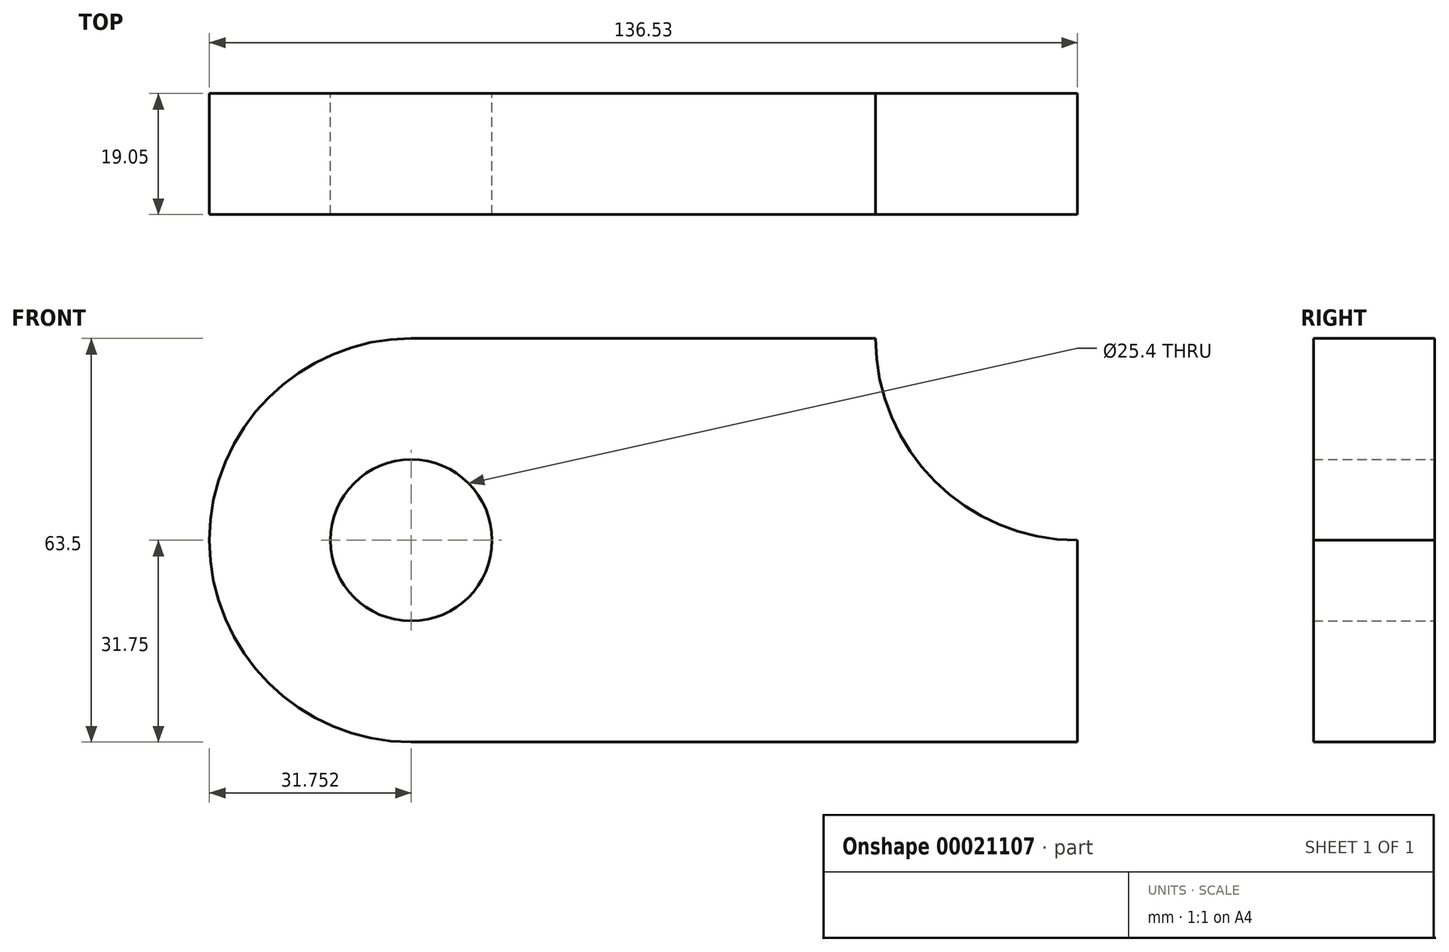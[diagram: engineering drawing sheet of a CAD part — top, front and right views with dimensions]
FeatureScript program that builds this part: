
annotation { "Feature Type Name" : "Feature", "Feature Type Description" : "" }
export const myFeature = defineFeature(function(context is Context, id is Id, definition is map)
    precondition{}
    {
        {
            var Q0;
            Q0=qCreatedBy(makeId("Front.planeOp"),FACE);
            var sketch = newSketch(context, id + "F0", { "sketchPlane" : qUnion([Q0])});
            skLineSegment(sketch, "E0.rect.bottom", {"start": v(52.39, 31.75) * mm, "end": v(-52.39, 31.75) * mm});
            skLineSegment(sketch, "E0.rect.top", {"start": v(52.39, -31.75) * mm, "end": v(-52.39, -31.75) * mm});
            skLineSegment(sketch, "E0.rect.left", {"start": v(52.39, 31.75) * mm, "end": v(52.39, -31.75) * mm});
            skLineSegment(sketch, "E0.rect.right", {"start": v(-52.39, 31.75) * mm, "end": v(-52.39, -31.75) * mm});
            skPoint(sketch, "E0.rect.middle", {"position": v(0, 0) * mm});
            skCircle(sketch, "E1", {"center": v(-52.39, 0) * mm, "radius": 31.75 * mm});
            skCircle(sketch, "E2", {"center": v(52.39, 31.75) * mm, "radius": 31.75 * mm});
            skCircle(sketch, "E3", {"center": v(-52.39, 0) * mm, "radius": 12.7 * mm});
            skSolve(sketch);
        }
        {
            var Q0;
            {var subQ3=sQuery(id+"F0.wireOp",EDGE,"E0.rect.bottom");var subQ6=sQuery(id+"F0.wireOp",EDGE,"E2");var subQ9=makeQuery(id+"F0.imprint","INTERSECT",VERTEX,{"derivedFrom":[subQ3,subQ6]});Q0=makeQuery(id+"F0.imprint","IMPRINT",FACE,{"disambiguationData":[TD([[makeQuery(id+"F0.imprint","IMPRINT",EDGE,{"disambiguationData":[TD([[subQ9,-1.0]])],"derivedFrom":subQ3}),1.0]])]});}
            var Q1;
            {var subQ1=sQuery(id+"F0.wireOp",EDGE,"E0.rect.right");var subQ7=sQuery(id+"F0.wireOp",EDGE,"E0.rect.bottom");var subQ10=makeQuery(id+"F0.imprint","INTERSECT",VERTEX,{"derivedFrom":[subQ7,subQ1]});Q1=makeQuery(id+"F0.imprint","IMPRINT",FACE,{"disambiguationData":[TD([[makeQuery(id+"F0.imprint","IMPRINT",EDGE,{"disambiguationData":[TD([[subQ10,1.0]])],"derivedFrom":subQ7}),1.0]])]});}
            var Q2;
            {var subQ1=sQuery(id+"F0.wireOp",EDGE,"E0.rect.right");var subQ7=sQuery(id+"F0.wireOp",EDGE,"E0.rect.bottom");var subQ10=makeQuery(id+"F0.imprint","INTERSECT",VERTEX,{"derivedFrom":[subQ7,subQ1]});Q2=makeQuery(id+"F0.imprint","IMPRINT",FACE,{"disambiguationData":[TD([[makeQuery(id+"F0.imprint","IMPRINT",EDGE,{"disambiguationData":[TD([[subQ10,1.0]])],"derivedFrom":subQ7}),-1.0]])]});}
            var Q3;
            {var subQ0=sQuery(id+"F0.wireOp",EDGE,"E3");var subQ1=sQuery(id+"F0.wireOp",EDGE,"E0.rect.right");var subQ3=makeQuery(id+"F0.imprint","INTERSECT",VERTEX,{"disambiguationData":[OD(0.0)],"derivedFrom":[subQ1,subQ0]});Q3=makeQuery(id+"F0.imprint","IMPRINT",FACE,{"disambiguationData":[TD([[makeQuery(id+"F0.imprint","IMPRINT",EDGE,{"disambiguationData":[TD([[subQ3,-1.0]])],"derivedFrom":subQ0}),-1.0]])]});}
            var Q4;
            {var subQ0=sQuery(id+"F0.wireOp",EDGE,"E3");var subQ1=sQuery(id+"F0.wireOp",EDGE,"E0.rect.right");var subQ3=makeQuery(id+"F0.imprint","INTERSECT",VERTEX,{"disambiguationData":[OD(0.0)],"derivedFrom":[subQ1,subQ0]});Q4=makeQuery(id+"F0.imprint","IMPRINT",FACE,{"disambiguationData":[TD([[makeQuery(id+"F0.imprint","IMPRINT",EDGE,{"disambiguationData":[TD([[subQ3,1.0]])],"derivedFrom":subQ0}),-1.0]])]});}
            extrude(context, id + "F1", {"entities" : qUnion([Q0, Q1, Q2, Q3, Q4]), "depth" : 19.05 * mm});
        }
    });
